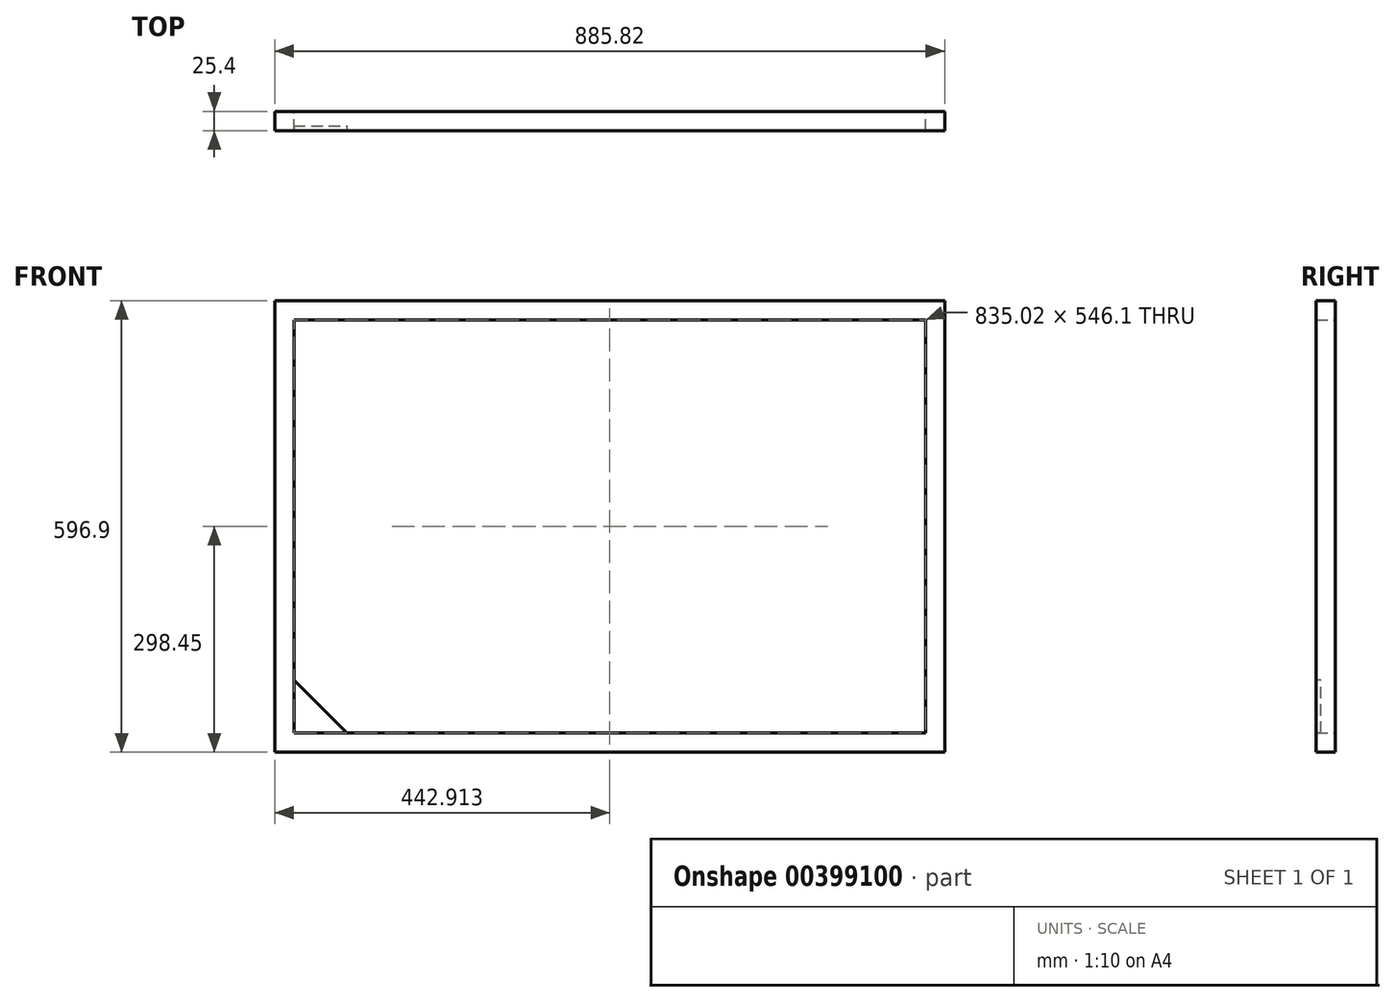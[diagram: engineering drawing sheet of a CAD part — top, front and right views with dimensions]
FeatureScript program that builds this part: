
annotation { "Feature Type Name" : "Feature", "Feature Type Description" : "" }
export const myFeature = defineFeature(function(context is Context, id is Id, definition is map)
    precondition{}
    {
        {
            var Q0;
            Q0=qCreatedBy(makeId("Front.planeOp"),FACE);
            var sketch = newSketch(context, id + "F0", { "sketchPlane" : qUnion([Q0])});
            skLineSegment(sketch, "E0", {"start": v(0, 0) * mm, "end": v(885.83, 0) * mm});
            skLineSegment(sketch, "E1", {"start": v(885.83, 0) * mm, "end": v(885.83, 596.9) * mm});
            skLineSegment(sketch, "E2", {"start": v(885.83, 596.9) * mm, "end": v(0, 596.9) * mm});
            skLineSegment(sketch, "E3", {"start": v(0, 596.9) * mm, "end": v(0, 0) * mm});
            skLineSegment(sketch, "E4", {"start": v(25.4, 571.5) * mm, "end": v(25.4, 25.4) * mm});
            skLineSegment(sketch, "E5", {"start": v(25.4, 25.4) * mm, "end": v(860.43, 25.4) * mm});
            skLineSegment(sketch, "E6", {"start": v(860.43, 25.4) * mm, "end": v(860.43, 571.5) * mm});
            skLineSegment(sketch, "E7", {"start": v(860.43, 571.5) * mm, "end": v(25.4, 571.5) * mm});
            skPoint(sketch, "E8.orphan", {"position": v(25.4, 0) * mm});
            skSolve(sketch);
        }
        {
            var Q0;
            Q0=qSketchRegion(id+"F0",true);
            extrude(context, id + "F1", {"entities" : qUnion([Q0]), "depth" : 25.4 * mm});
        }
        {
            var Q0;
            Q0=makeQuery(id+"F1.opExtrude","CAP_FACE",FACE,{"disambiguationData":[OSD([sQuery(id+"F0.wireOp",EDGE,"E0"),sQuery(id+"F0.wireOp",EDGE,"E1"),sQuery(id+"F0.wireOp",EDGE,"E2"),sQuery(id+"F0.wireOp",EDGE,"E3"),sQuery(id+"F0.wireOp",EDGE,"E4"),sQuery(id+"F0.wireOp",EDGE,"E5"),sQuery(id+"F0.wireOp",EDGE,"E6"),sQuery(id+"F0.wireOp",EDGE,"E7")])],"isStart":false});
            var sketch = newSketch(context, id + "F2", { "sketchPlane" : qUnion([Q0])});
            skLineSegment(sketch, "E9", {"start": v(25.4, 25.4) * mm, "end": v(25.4, 95.25) * mm});
            skLineSegment(sketch, "E10", {"start": v(25.4, 25.4) * mm, "end": v(95.25, 25.4) * mm});
            skLineSegment(sketch, "E11", {"start": v(95.25, 25.4) * mm, "end": v(25.4, 95.25) * mm});
            skSolve(sketch);
        }
        {
            var Q0;
            Q0=qSketchRegion(id+"F2",true);
            extrude(context, id + "F3", {"entities" : qUnion([Q0]), "oppositeDirection" : true, "depth" : 6.35 * mm});
        }
    });
